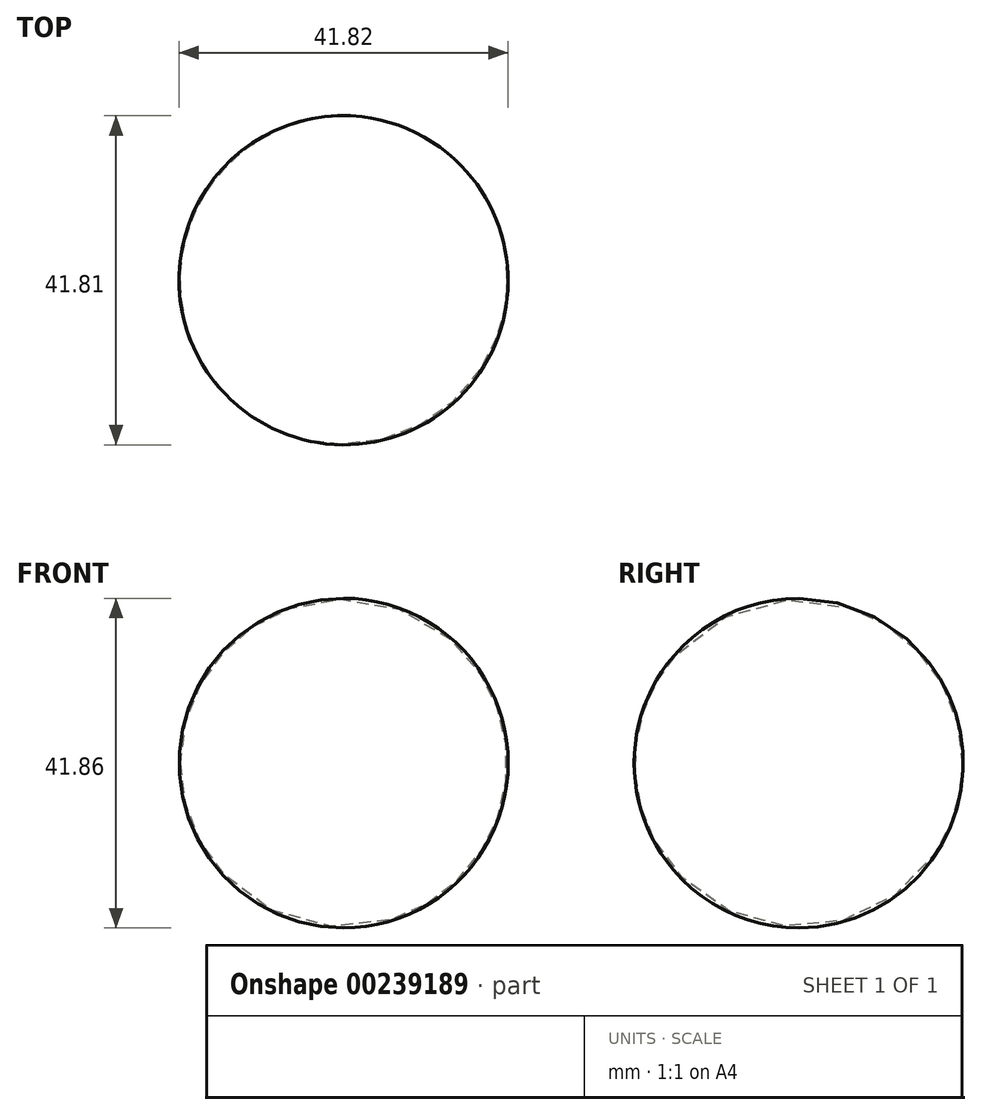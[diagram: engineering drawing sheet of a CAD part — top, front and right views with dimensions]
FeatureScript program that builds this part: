
annotation { "Feature Type Name" : "Feature", "Feature Type Description" : "" }
export const myFeature = defineFeature(function(context is Context, id is Id, definition is map)
    precondition{}
    {
        {
            var Q0;
            Q0=qCreatedBy(makeId("Top.planeOp"),FACE);
            var sketch = newSketch(context, id + "F0", { "sketchPlane" : qUnion([Q0])});
            skArc(sketch, "E0", {"start": v(-14.2, -15.26) * mm, "mid": v(15.31, -14.14) * mm, "end": v(14.08, 15.37) * mm});
            skLineSegment(sketch, "E1", {"start": v(0, 0) * mm, "end": v(-0.06, 0.05) * mm});
            skLineSegment(sketch, "E2", {"start": v(16.8, -12.33) * mm, "end": v(18.02, -13.22) * mm});
            skLineSegment(sketch, "E3", {"start": v(-14.2, -15.26) * mm, "end": v(14.08, 15.37) * mm});
            skSolve(sketch);
        }
        {
            var Q0;
            {var subQ1=sQuery(id+"F0.wireOp",EDGE,"E0");var subQ3=makeQuery(id+"F0.imprint","IMPRINT",VERTEX,{"derivedFrom":subQ1});Q0=makeQuery(id+"F0.imprint","IMPRINT",FACE,{"disambiguationData":[TD([[makeQuery(id+"F0.imprint","IMPRINT",EDGE,{"disambiguationData":[TD([[subQ3,1.0]])],"derivedFrom":subQ1}),1.0]])]});}
            var Q1;
            Q1=sQuery(id+"F0.wireOp",EDGE,"E3");
            revolve(context, id + "F1", {"entities" : qUnion([Q0]), "axis" : qUnion([Q1]), "revolveType" : RevolveType.FULL});
        }
    });
